# Revit family: Arper_CatifaSensit_Direction_chair_5ways_4905
name_source: partatom
category: Arredi
revit_build: Autodesk Revit 2016 (Build: 20151007_0715(x64)
units: mm (PartAtom-declared; Revit-internal decimal feet)

## family parameters
Basato su piano di lavoro = No
Condiviso = No
Numero OmniClass = 23.40.20.00
Punto di calcolo locali = No
Sempre verticale = Sì
Taglio con vuoti quando caricato = No
Titolo OmniClass = General Furniture and Specialties

## types (1)
- Arper_CatifaSensit_Direction_chair_5ways_4905
    Descrizione = Chair with polished or powdercoated aluminum 5 way swivel base on
castors, fitted with gas-lift mechanism for height adjustment. Shell
with high backrest, entirely upholstered in leather, customer's
leather, faux leather, fabric or customer's fabric and  fitted with self-
tensioning weight response mechanism. Aluminium armrests are
offered in the same finishes of the base (BI) or upholstered (BR).
    Modello = Catifa Sensit
    Produttore = ARPER s.p.a.
    URL = http://www.arper.com
